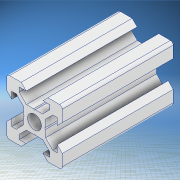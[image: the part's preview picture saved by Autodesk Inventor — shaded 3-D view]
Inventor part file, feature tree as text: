
AUTODESK INVENTOR PART (.ipt)
format: ipt  version: 2020.2 (Build 242310000, 310)  size: 190,976 bytes
history: native  units: mm
features: extrude x1, sketch x1
ambient origin geometry x8: Origin, YZ Plane, XZ Plane, XY Plane, X Axis, Y Axis, Z Axis, Center Point
bodies: Solid1 (feature_tree)
feature tree (2):
  extrude  "Extrusion1"  Depth=40.0mm TaperAngle=0.0deg
  sketch  "Sketch1"  dims[d1=40.0mm d2=360.0deg d3=40.0mm d4=0.0mm]
